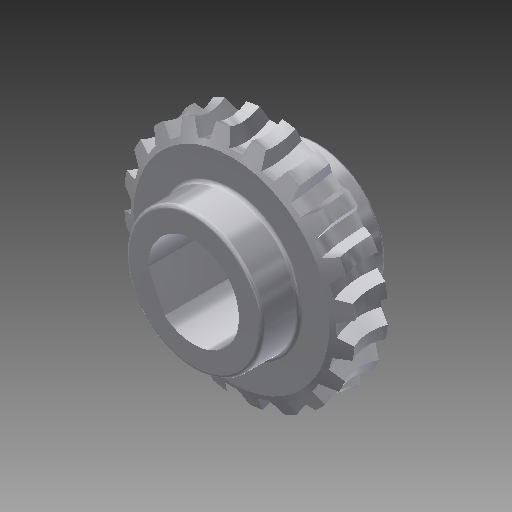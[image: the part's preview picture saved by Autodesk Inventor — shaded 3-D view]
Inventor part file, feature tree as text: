
AUTODESK INVENTOR PART (.ipt)
format: ipt  version: 2019 (Build 230136000, 136)  size: 432,640 bytes
history: native  units: mm (DEFAULTED — no unit token found)
features: other x6, extrude x3, sketch x3, plane x2, reference x2, pattern_circular x1, mirror x1, fillet x1
ambient origin geometry x5: Origin, X Axis, Y Axis, Z Axis, Center Point
bodies: Solid1 (feature_tree)
feature tree (19):
  other  "Tooth Plane"
  other  "Base Body"
  other  "Tooth"
  pattern_circular  "Tooth Pattern"  Count=4  [1 undecoded]
  plane  "Work Plane15"
  plane  "Work Plane16"
  extrude  "Extrusion1"  Depth=0.5mm
  extrude  "Extrusion2"  Depth=10.0mm
  mirror  "Mirror1"
  fillet  "Fillet1"  Radius=3.490659mm
  other  "Base Body Sketch"
  other  "Tooth Sketch"
  sketch  "Sketch10"  dims[d2=36.792mm]
  other  "Srf1"
  sketch  "Sketch11"  dims[d4=60.0deg]
  reference  "Reference1"
  reference  "Reference2"
  sketch  "Sketch12"  dims[d6=30.0deg d8=40.0mm d10=14.0mm d12=10.0mm d15=0.0mm d17=3.490659mm d19=9.0mm d21=13.635mm d23=2.35mm d25=11.5mm d27=0.0mm d30=8.640804mm d31=5.174446mm d32=6.5mm d33=20.0mm d35=90.0deg d36=1.22173mm d37=-0.996687mm d38=20.0mm d39=3.490659mm d40=4.915723mm d41=6.0mm d42=1.2192mm d43=90.0deg d44=200.0mm d46=360.0deg d50=4.320402mm d69=20.0mm d74=0.0mm d81=27.0mm d82=6.5mm d83=0.0mm d87=0.0mm d88=0.0mm d89=0.0mm d91=1.570796mm d94=180.0deg d95=20.0mm d96=0.0mm d97=0.0mm d99=10.0mm d100=0.0mm d101=0.1mm d103=18.0mm d104=5.0mm d105=0.0mm d106=0.5mm]
  extrude  "ExtrusionSrf1"  Depth=9.0mm
note: 1 required parameter value undecoded (feature->parameter linkage not recoverable at this tier; creation-order binding heuristic only, values carry confidence <= 0.55)
